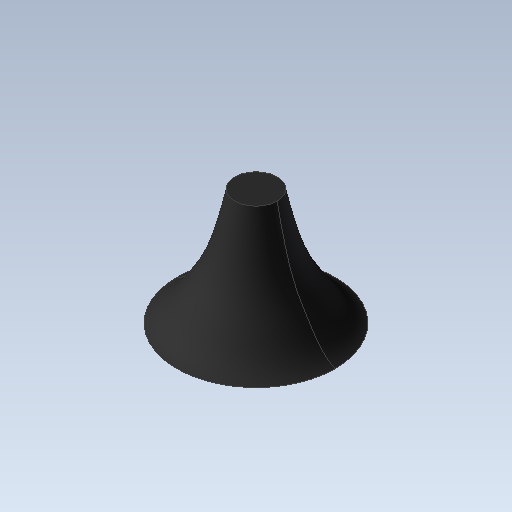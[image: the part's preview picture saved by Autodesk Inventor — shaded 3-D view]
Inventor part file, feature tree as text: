
AUTODESK INVENTOR PART (.ipt)
format: ipt  version: 2020 (Build 240168000, 168)  size: 141,312 bytes
history: native  units: in
note: dims shown in document units (in); Inventor stores cm internally (conversion verified against a paired STEP export)
features: revolve x1
ambient origin geometry x8: Origin, YZ Plane, XZ Plane, XY Plane, X Axis, Y Axis, Z Axis, Center Point
bodies: Solid1 (feature_tree)
feature tree (1):
  revolve  "Revolve1"  [1 undecoded]
note: 1 required parameter value undecoded (feature->parameter linkage not recoverable at this tier; creation-order binding heuristic only, values carry confidence <= 0.55)
